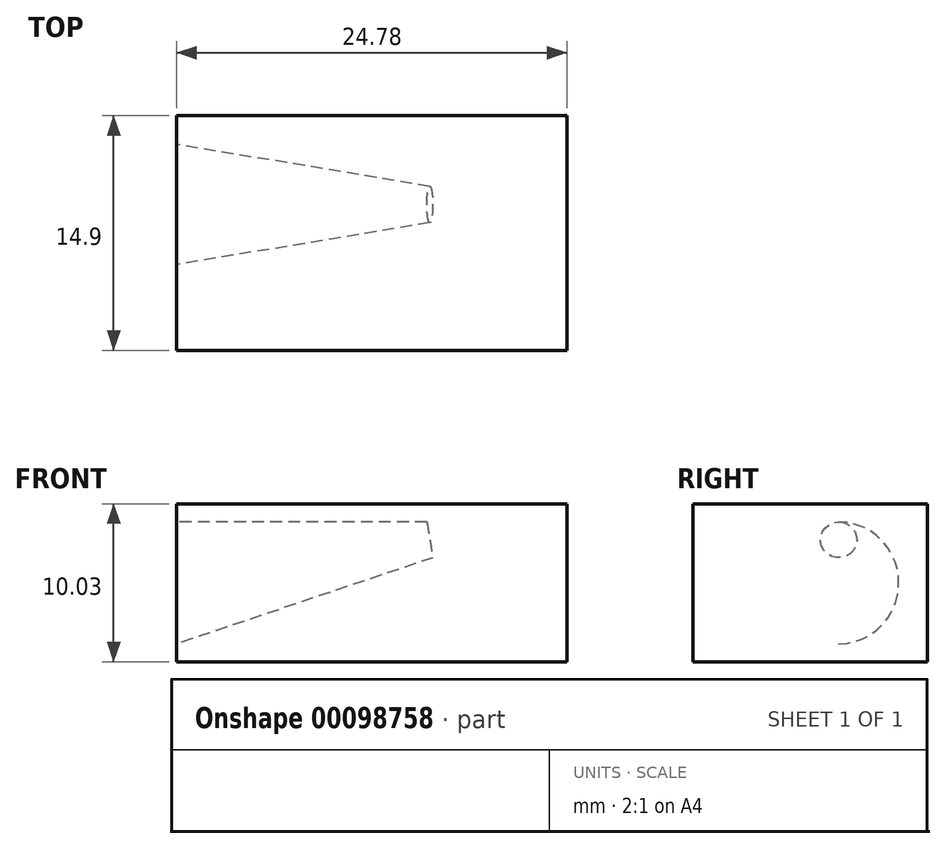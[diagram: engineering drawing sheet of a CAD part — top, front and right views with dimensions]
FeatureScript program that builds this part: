
annotation { "Feature Type Name" : "Feature", "Feature Type Description" : "" }
export const myFeature = defineFeature(function(context is Context, id is Id, definition is map)
    precondition{}
    {
        {
            var Q0;
            Q0=qCreatedBy(makeId("Front.planeOp"),FACE);
            var sketch = newSketch(context, id + "F0", { "sketchPlane" : qUnion([Q0])});
            skLineSegment(sketch, "E0", {"start": v(-24.78, 0) * mm, "end": v(0, 0) * mm});
            skLineSegment(sketch, "E1", {"start": v(0, 0) * mm, "end": v(0, 10.03) * mm});
            skLineSegment(sketch, "E2", {"start": v(0, 10.03) * mm, "end": v(-24.78, 10.03) * mm});
            skLineSegment(sketch, "E3", {"start": v(-24.78, 10.03) * mm, "end": v(-24.78, 0) * mm});
            skSolve(sketch);
        }
        {
            var Q0;
            Q0 = qSketchRegion(id + "F0", true);
            extrude(context, id + "F1", {"entities" : qUnion([Q0]), "depth" : 14.9 * mm});
        }
        {
            var Q0;
            Q0=makeQuery(id+"F0.imprint","IMPRINT",FACE,{"disambiguationData":[TD([[makeQuery(id+"F0.imprint","IMPRINT",EDGE,{"derivedFrom":sQuery(id+"F0.wireOp",EDGE,"E0")}),1.0]])]});
            cPlane(context, id + "F2", {"entities" : qUnion([Q0]), "cplaneType" : CPlaneType.OFFSET, "offset" : 5.64 * mm, "width" : 150 * mm, "height" : 150 * mm});
        }
        {
            var Q0;
            Q0=qCreatedBy(id+"F2.planeOp",FACE);
            var sketch = newSketch(context, id + "F3", { "sketchPlane" : qUnion([Q0])});
            skLineSegment(sketch, "E4", {"start": v(-8.9, 8.87) * mm, "end": v(-26.66, 8.87) * mm});
            skLineSegment(sketch, "E5", {"start": v(-8.7, 7.74) * mm, "end": v(-26.01, 4.9) * mm});
            skLineSegment(sketch, "E6", {"start": v(-26.01, 4.9) * mm, "end": v(-26.66, 8.87) * mm});
            skLineSegment(sketch, "E7", {"start": v(-8.9, 8.87) * mm, "end": v(-8.7, 7.74) * mm});
            skSolve(sketch);
        }
        {
            var Q0;
            Q0 = qSketchRegion(id + "F3", true);
            var Q1;
            Q1=sQuery(id+"F3.wireOp",EDGE,"E5");
            revolve(context, id + "F4", {"operationType" : NewBodyOperationType.REMOVE, "entities" : qUnion([Q0]), "axis" : qUnion([Q1]), "revolveType" : RevolveType.FULL, "oppositeDirection" : true});
        }
    });
